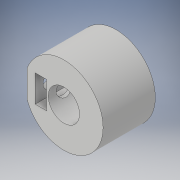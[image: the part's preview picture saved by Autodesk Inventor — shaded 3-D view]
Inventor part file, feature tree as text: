
AUTODESK INVENTOR PART (.ipt)
format: ipt  version: 2019 (Build 230136000, 136)  size: 136,704 bytes
history: native  units: mm
features: sketch x5, extrude x4, plane x1
ambient origin geometry x8: Origin, YZ Plane, XZ Plane, XY Plane, X Axis, Y Axis, Z Axis, Center Point
bodies: Solid1 (feature_tree)
feature tree (10):
  extrude  "Extrusion1"  Depth=6.0mm
  plane  "Work Plane1"
  extrude  "Extrusion2"  Depth=10.0mm
  extrude  "Extrusion3"  Depth=2.2mm
  extrude  "Extrusion4"  Depth=7.0mm TaperAngle=0.0deg
  sketch  "Sketch6"  dims[d12=3.0mm d13=7.0mm d14=8.0mm d15=0.0mm d16=6.0mm d17=10.0mm d18=0.5mm d19=8.0mm d20=0.0mm]
  sketch  "Sketch1"  dims[d0=15.0mm d1=6.0mm]
  sketch  "Sketch2"  dims[d2=10.0mm d3=0.0mm d4=3.0mm]
  sketch  "Sketch4"  dims[d5=5.5mm d6=2.2mm]
  sketch  "Sketch5"  dims[d7=5.2mm d8=7.0mm d9=0.0mm]
